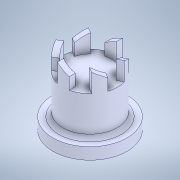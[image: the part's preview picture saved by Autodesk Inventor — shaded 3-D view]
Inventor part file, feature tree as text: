
AUTODESK INVENTOR PART (.ipt)
format: ipt  version: 2022 (Build 260153000, 153)  size: 175,616 bytes
history: mixed  units: mm
features: fillet x1, imported_body x1
ambient origin geometry x8: Origin, YZ Plane, XZ Plane, XY Plane, X Axis, Y Axis, Z Axis, Center Point
bodies: Solid1 (imported_parasolid)
feature tree (2):
  fillet  "Fillet1"  [1 undecoded]
  imported_body  NMx_Import_Brep_tag  [imported B-rep: ~33 faces, bbox_mm=[13.351491, 17.748436, 16.334269]]
note: 1 required parameter value undecoded (feature->parameter linkage not recoverable at this tier; creation-order binding heuristic only, values carry confidence <= 0.55)
